# Revit family: 2842_Intrinsically Safe Barrier Unit
name_source: partatom
category: Fire Alarm Devices
units: mm (PartAtom-declared; Revit-internal decimal feet)

## family parameters
Cut with Voids When Loaded = No
Host = Face
Maintain Annotation Orientation = No
OmniClass Number = 23.85.30.21
OmniClass Title = Environmental Detection/Registration
Part Type = Normal
Room Calculation Point = No
Round Connector Dimension = Use Diameter
Shared = No

## types (1)
- 2842
    ATEX Certificate = DEKRA 11ATEX0106
    ATEX Classification = I (1) G [Ex ia Ga] IIC
    Ambient Humidity = Maximum 95 % RH
    Ambient Temperature Operating = -10 to +55 °C
    Ambient Temperature Storage = -25 to +70 °C
    CPR = 2831-CPR-F2577
    Current COM Loop = ≤ 10 mA
    Current Power Supply = ≤ 50 mA
    Default Elevation = 0 mm  [stored 0 ft]
    Depth (mm) = 132 mm  [stored 0.433071 ft]
    Description = Intrinsically safe barrier unit 2842
    Height (mm) = 300 mm
    IS COM line = For example: FKAR-PG 2 x 0.5 mm², blue
    Ingress Protection Rating = IP 66/67
    Manufacturer = Panasonic
    Max_Wire Size = Ø 1.2 mm (1.13 mm²)
    Min_Wire Size = Ø 0.6 mm (0.3 mm²)
    Model = 2842
    Omniclass Code = 23.85.30.21.11.11.11
    Omniclass Description = Smoke Detectors
    Product Material = FR ABS and polycarbonate_Panasonic_Grey
    Tested and Approved = EN54-18
    Type Comments = The intrinsically safe barrier 2842 unit is used to connect analog addressable IS detectors (2840 and 2841) to the COM loop. Up to 20 IS detectors can be connected on the IS COM line, which is a single line with no return cable and no end-of-line device.
    URL = https://www.panasonic-fire-security.com
    Uniclass 2015 Code = Pr_75_80_30_27
    Uniclass 2015 Description = Fire and smoke detector bases
    Uniformat 2010  Code = D7050
    Uniformat 2010 Description = Detection and Alarm
    Version = RVT20
    Voltage Allowed = 12-30 VDC
    Voltage Normal = 24 VDC
    Weight = 3100 g
    Width (mm) = 300 mm
    Zone Classification = Non-Hazardous Area

note: [stored X ft] marks values corroborated as IEEE doubles in the binary element streams (Revit-internal decimal feet)

## geometry (parser evidence)
native form markers: Blend x85, Sweep x2
no freeform markers — native parametric forms only
